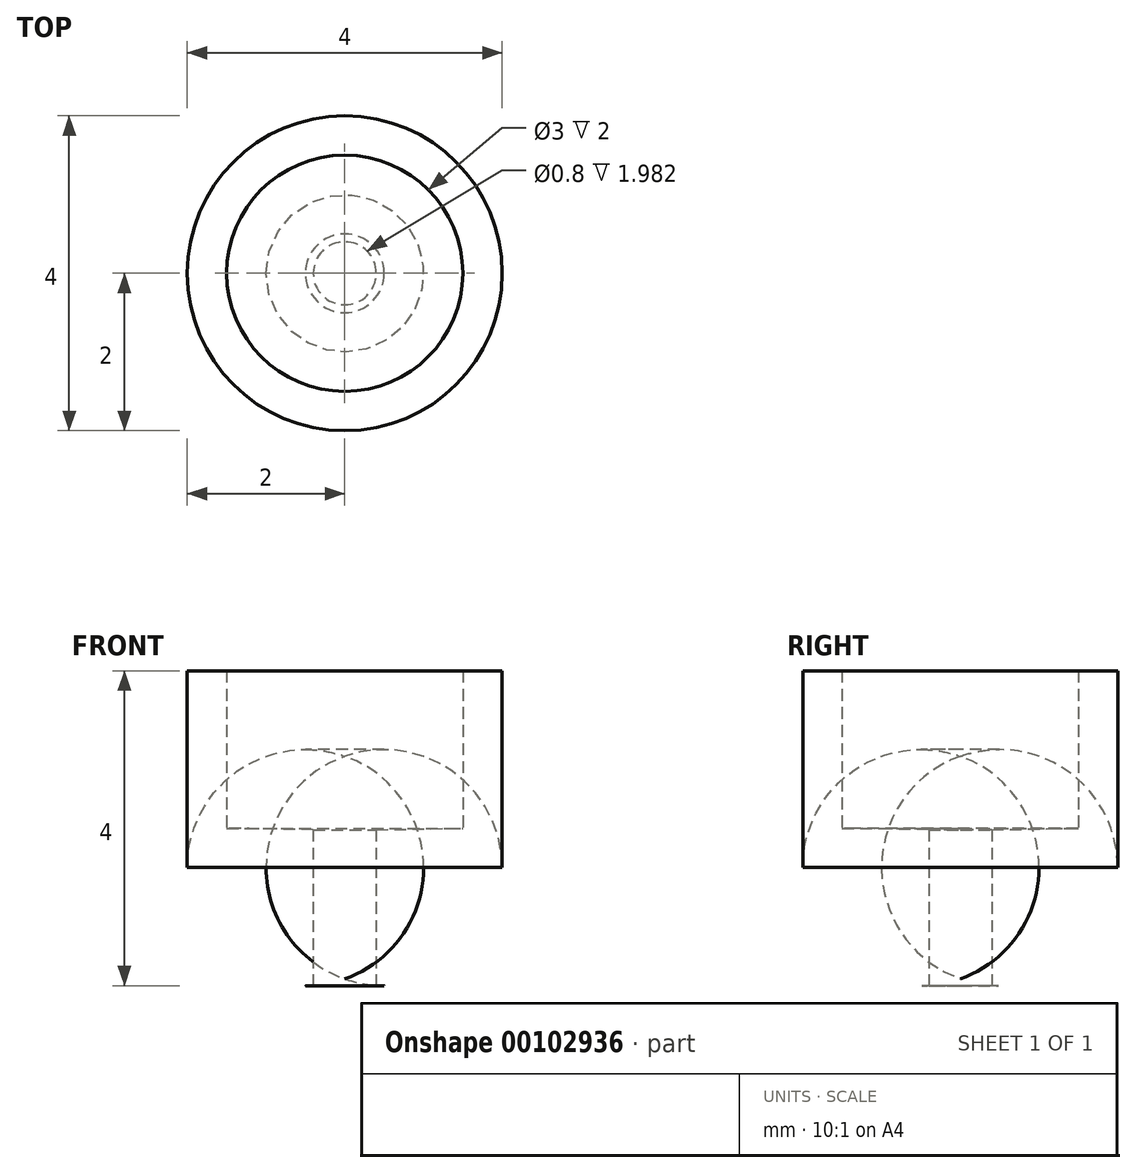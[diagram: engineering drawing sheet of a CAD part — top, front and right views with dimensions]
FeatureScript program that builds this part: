
annotation { "Feature Type Name" : "Feature", "Feature Type Description" : "" }
export const myFeature = defineFeature(function(context is Context, id is Id, definition is map)
    precondition{}
    {
        {
            var Q0;
            Q0=qCreatedBy(makeId("Front.planeOp"),FACE);
            var sketch = newSketch(context, id + "F0", { "sketchPlane" : qUnion([Q0])});
            skLineSegment(sketch, "E0", {"start": v(-2, 0) * mm, "end": v(-2, 4) * mm});
            skLineSegment(sketch, "E1", {"start": v(-2, 4) * mm, "end": v(-1.5, 4) * mm});
            skLineSegment(sketch, "E2", {"start": v(-1.5, 4) * mm, "end": v(-1.5, 2) * mm});
            skLineSegment(sketch, "E3", {"start": v(-2, 0) * mm, "end": v(-0.4, 0) * mm});
            skLineSegment(sketch, "E4", {"start": v(-0.4, 0) * mm, "end": v(-0.4, 1.98) * mm});
            skLineSegment(sketch, "E5", {"start": v(-0.4, 1.98) * mm, "end": v(-1.5, 2) * mm});
            skLineSegment(sketch, "E6", {"start": v(0, -1.58) * mm, "end": v(0, 5.25) * mm, "construction": true});
            skSolve(sketch);
        }
        {
            var Q0;
            Q0=makeQuery(id+"F0.imprint","IMPRINT",FACE,{"disambiguationData":[TD([[makeQuery(id+"F0.imprint","IMPRINT",EDGE,{"derivedFrom":sQuery(id+"F0.wireOp",EDGE,"E0")}),-1.0]])]});
            var Q1;
            Q1=sQuery(id+"F0.wireOp",EDGE,"E6");
            revolve(context, id + "F1", {"entities" : qUnion([Q0]), "axis" : qUnion([Q1]), "revolveType" : RevolveType.FULL});
        }
        {
            var Q0;
            Q0=makeQuery(id+"F1.opRevolve","SWEPT_EDGE",EDGE,{"disambiguationData":[OSD([sQuery(id+"F0.wireOp",EDGE,"E0"),sQuery(id+"F0.wireOp",EDGE,"E3")])]});
            fillet(context, id + "F2", {"entities" : qUnion([Q0]), "radius" : 1.5 * mm, "tangentPropagation" : true, "allowEdgeOverflow" : false});
        }
    });
